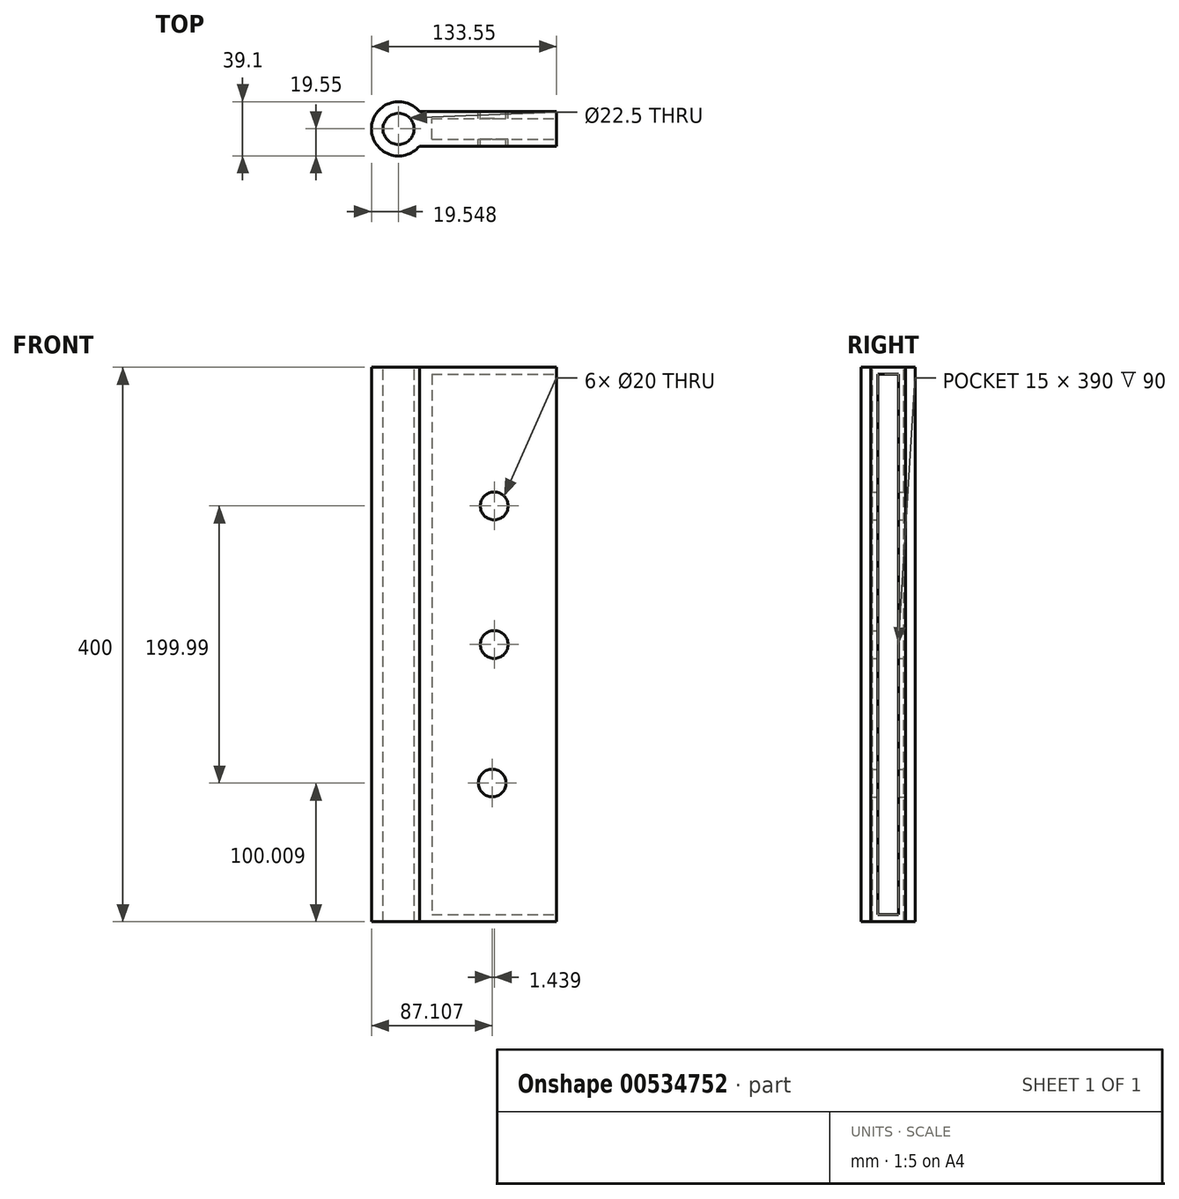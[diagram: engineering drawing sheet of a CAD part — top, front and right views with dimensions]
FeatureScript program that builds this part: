
annotation { "Feature Type Name" : "Feature", "Feature Type Description" : "" }
export const myFeature = defineFeature(function(context is Context, id is Id, definition is map)
    precondition{}
    {
        {
            var Q0;
            Q0=qCreatedBy(makeId("Front.planeOp"),FACE);
            var sketch = newSketch(context, id + "F0", { "sketchPlane" : qUnion([Q0])});
            skLineSegment(sketch, "E0.bottom", {"start": v(-403.22, 96.72) * mm, "end": v(-303.22, 96.72) * mm});
            skLineSegment(sketch, "E0.top", {"start": v(-403.22, -303.28) * mm, "end": v(-303.22, -303.28) * mm});
            skLineSegment(sketch, "E0.left", {"start": v(-403.22, 96.72) * mm, "end": v(-403.22, -303.28) * mm});
            skLineSegment(sketch, "E0.right", {"start": v(-303.22, 96.72) * mm, "end": v(-303.22, -303.28) * mm});
            skSolve(sketch);
        }
        {
            var Q0;
            Q0=makeQuery(id+"F0.imprint","IMPRINT",FACE,{"disambiguationData":[TD([[makeQuery(id+"F0.imprint","IMPRINT",EDGE,{"derivedFrom":sQuery(id+"F0.wireOp",EDGE,"E0.bottom")}),-1.0]])]});
            extrude(context, id + "F1", {"entities" : qUnion([Q0]), "depth" : 25 * mm, "offsetDistance" : 25 * mm});
        }
        {
            var Q0;
            Q0=makeQuery(id+"F1.opExtrude","SWEPT_FACE",FACE,{"disambiguationData":[OSD([sQuery(id+"F0.wireOp",EDGE,"E0.right")])]});
            var sketch = newSketch(context, id + "F2", { "sketchPlane" : qUnion([Q0])});
            skLineSegment(sketch, "E1.bottom", {"start": v(-20, 91.72) * mm, "end": v(-5, 91.72) * mm});
            skLineSegment(sketch, "E1.top", {"start": v(-20, -298.28) * mm, "end": v(-5, -298.28) * mm});
            skLineSegment(sketch, "E1.left", {"start": v(-20, 91.72) * mm, "end": v(-20, -298.28) * mm});
            skLineSegment(sketch, "E1.right", {"start": v(-5, 91.72) * mm, "end": v(-5, -298.28) * mm});
            skSolve(sketch);
        }
        {
            var Q0;
            Q0=makeQuery(id+"F2.imprint","IMPRINT",FACE,{"disambiguationData":[TD([[makeQuery(id+"F2.imprint","IMPRINT",EDGE,{"derivedFrom":sQuery(id+"F2.wireOp",EDGE,"E1.bottom")}),-1.0]])]});
            extrude(context, id + "F3", {"entities" : qUnion([Q0]), "operationType" : NewBodyOperationType.REMOVE, "oppositeDirection" : true, "depth" : 90 * mm, "offsetDistance" : 25 * mm});
        }
        {
            var Q0;
            Q0=makeQuery(id+"F1.opExtrude","CAP_FACE",FACE,{"disambiguationData":[OSD([sQuery(id+"F0.wireOp",EDGE,"E0.bottom"),sQuery(id+"F0.wireOp",EDGE,"E0.top"),sQuery(id+"F0.wireOp",EDGE,"E0.left"),sQuery(id+"F0.wireOp",EDGE,"E0.right")])],"isStart":true});
            var sketch = newSketch(context, id + "F4", { "sketchPlane" : qUnion([Q0])});
            skCircle(sketch, "E2", {"center": v(348.22, -3.28) * mm, "radius": 10 * mm});
            skCircle(sketch, "E3", {"center": v(348.22, -103.28) * mm, "radius": 10 * mm});
            skCircle(sketch, "E4", {"center": v(349.66, -203.27) * mm, "radius": 10 * mm});
            skSolve(sketch);
        }
        {
            var Q0;
            Q0 = qSketchRegion(id + "F4", true);
            extrude(context, id + "F5", {"entities" : qUnion([Q0]), "operationType" : NewBodyOperationType.REMOVE, "oppositeDirection" : true, "depth" : 1000 * mm, "offsetDistance" : 25 * mm});
        }
        {
            var Q0;
            Q0=makeQuery(id+"F1.opExtrude","SWEPT_FACE",FACE,{"disambiguationData":[OSD([sQuery(id+"F0.wireOp",EDGE,"E0.bottom")])]});
            var sketch = newSketch(context, id + "F6", { "sketchPlane" : qUnion([Q0])});
            skCircle(sketch, "E5", {"center": v(-417.22, -12.5) * mm, "radius": 19.55 * mm});
            skPoint(sketch, "E5.centerSnap0", {"position": v(-403.22, -12.5) * mm});
            skSolve(sketch);
        }
        {
            var Q0;
            {var subQ1=sQuery(id+"F0.wireOp",EDGE,"E0.bottom");var subQ6=makeQuery(id+"F1.opExtrude","SWEPT_EDGE",EDGE,{"disambiguationData":[OSD([subQ1,sQuery(id+"F0.wireOp",EDGE,"E0.left")])]});Q0=makeQuery(id+"F6.imprint","IMPRINT",FACE,{"disambiguationData":[TD([[makeQuery(id+"F6.imprint","IMPRINT",EDGE,{"derivedFrom":subQ6}),-1.0]])]});}
            var Q1;
            {var subQ1=sQuery(id+"F0.wireOp",EDGE,"E0.bottom");var subQ6=makeQuery(id+"F1.opExtrude","SWEPT_EDGE",EDGE,{"disambiguationData":[OSD([subQ1,sQuery(id+"F0.wireOp",EDGE,"E0.left")])]});Q1=makeQuery(id+"F6.imprint","IMPRINT",FACE,{"disambiguationData":[TD([[makeQuery(id+"F6.imprint","IMPRINT",EDGE,{"derivedFrom":subQ6}),1.0]])]});}
            extrude(context, id + "F7", {"entities" : qUnion([Q0, Q1]), "operationType" : NewBodyOperationType.ADD, "oppositeDirection" : true, "depth" : 400 * mm, "offsetDistance" : 25 * mm});
        }
        {
            var Q0;
            Q0=makeQuery(id+"F7.boolean.opBoolean","MERGE",FACE,{"derivedFrom":[makeQuery(id+"F1.opExtrude","SWEPT_FACE",FACE,{"disambiguationData":[OSD([sQuery(id+"F0.wireOp",EDGE,"E0.bottom")])]}),makeQuery(id+"F7.opExtrude","CAP_FACE",FACE,{"disambiguationData":[OSD([sQuery(id+"F6.wireOp",EDGE,"E5")])],"isStart":true})]});
            var sketch = newSketch(context, id + "F8", { "sketchPlane" : qUnion([Q0])});
            skCircle(sketch, "E6", {"center": v(-417.22, -12.5) * mm, "radius": 11.25 * mm});
            skSolve(sketch);
        }
        {
            var Q0;
            Q0=makeQuery(id+"F8.imprint","IMPRINT",FACE,{"disambiguationData":[TD([[makeQuery(id+"F8.imprint","IMPRINT",EDGE,{"derivedFrom":sQuery(id+"F8.wireOp",EDGE,"E6")}),1.0]])]});
            extrude(context, id + "F9", {"entities" : qUnion([Q0]), "operationType" : NewBodyOperationType.REMOVE, "oppositeDirection" : true, "depth" : 500 * mm, "offsetDistance" : 25 * mm});
        }
    });
